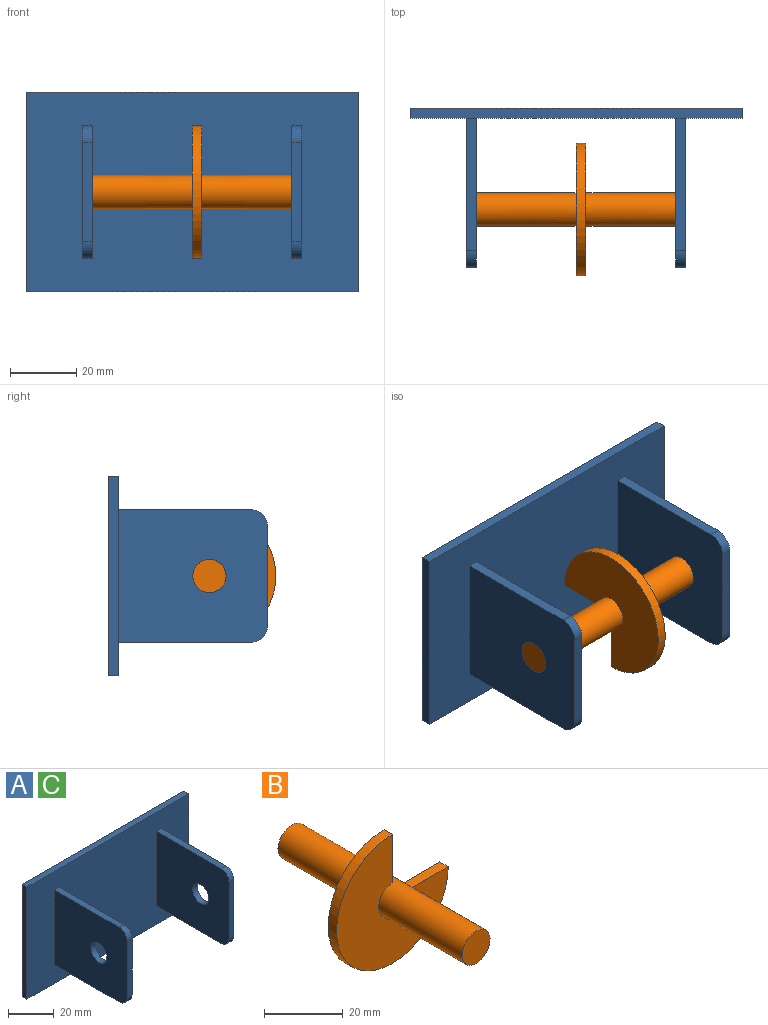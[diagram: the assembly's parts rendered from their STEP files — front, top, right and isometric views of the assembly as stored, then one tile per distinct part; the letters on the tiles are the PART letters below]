
ASSEMBLY  parts=3 mates=1
PART A: 22 faces, bbox 100x48x60 mm
  f0: plane 60x3mm, normal (1,0,0), area 180mm2, adj f1,f3,f4,f5
  f1: plane 100x3mm, normal (0,0,1), area 300mm2, adj f0,f2,f4,f5
  f2: plane 60x3mm, normal (-1,0,0), area 180mm2, adj f1,f3,f4,f5
  f3: plane 100x3mm, normal (0,0,-1), area 300mm2, adj f0,f2,f4,f5
  f4: plane 100x60mm, normal (0,-1,0), area 5760mm2, adj f0,f1,f2,f3,f6,f7,f8,f9
  f5: plane 100x60mm, normal (0,1,0), area 6000mm2, adj f0,f1,f2,f3
  f6: plane 40x3mm, normal (0,0,1), area 120mm2, adj f4,f7,f9,f21
  f7: plane 45x40mm, normal (-1,0,0), area 1710.7mm2, adj f4,f6,f8,f10,f17,f20,f21
  f8: plane 40x3mm, normal (0,0,-1), area 120mm2, adj f4,f7,f9,f20
  f9: plane 45x40mm, normal (1,0,0), area 1710.7mm2, adj f4,f6,f8,f10,f17,f20,f21
  f10: plane 30x3mm, normal (0,-1,0), area 90mm2, adj f7,f9,f20,f21
  f11: plane 45x40mm, normal (1,0,0), area 1710.7mm2, adj f4,f12,f14,f15,f16,f18,f19
  f12: plane 40x3mm, normal (0,0,1), area 120mm2, adj f4,f11,f13,f18
  f13: plane 45x40mm, normal (-1,0,0), area 1710.7mm2, adj f4,f12,f14,f15,f16,f18,f19
  f14: plane 40x3mm, normal (0,0,-1), area 120mm2, adj f4,f11,f13,f19
  f15: plane 30x3mm, normal (0,-1,0), area 90mm2, adj f11,f13,f18,f19
  f16: cylinder r=5mm len=10mm, axis (1,0,0), area 94.2mm2, adj f11,f13
  f17: cylinder r=5mm len=10mm, axis (1,0,0), area 94.2mm2, adj f7,f9
  f18: cylinder r=5mm len=5mm, axis (1,0,0), area 23.6mm2, adj f11,f12,f13,f15
  f19: cylinder r=5mm len=5mm, axis (-1,0,0), area 23.6mm2, adj f11,f13,f14,f15
  f20: cylinder r=5mm len=5mm, axis (-1,0,0), area 23.6mm2, adj f7,f8,f9,f10
  f21: cylinder r=5mm len=5mm, axis (1,0,0), area 23.6mm2, adj f6,f7,f9,f10
PART B: 8 faces, bbox 40x66x40 mm
  f0: cylinder r=20mm len=40mm, axis (0,1,0), area 282.7mm2, adj f1,f2,f3,f4
  f1: plane 15x3mm, normal (0,0,1), area 45mm2, adj f0,f3,f4,f5
  f2: plane 15x3mm, normal (1,0,0), area 45mm2, adj f0,f3,f4,f5
  f3: plane 40x40mm, normal (0,-1,0), area 883.6mm2, adj f0,f1,f2,f5
  f4: plane 40x40mm, normal (0,1,0), area 883.6mm2, adj f0,f1,f2,f5
  f5: cylinder r=5mm len=66mm, axis (0,1,0), area 2002.8mm2, adj f1,f2,f3,f4,f6,f7
  f6: plane 10x10mm, normal (0,-1,0), area 78.5mm2, adj f5
  f7: plane 10x10mm, normal (0,1,0), area 78.5mm2, adj f5
PART C: same geometry as A
PLACE A at identity
PLACE B rot(axis=(-0.58,0.58,0.58),120deg) t=(0,-30.5,0)mm
PLACE C at identity
MATE revolute B.f5 <-> A.f16  axis (-1,0,0) through (-33,-30.5,0)mm
